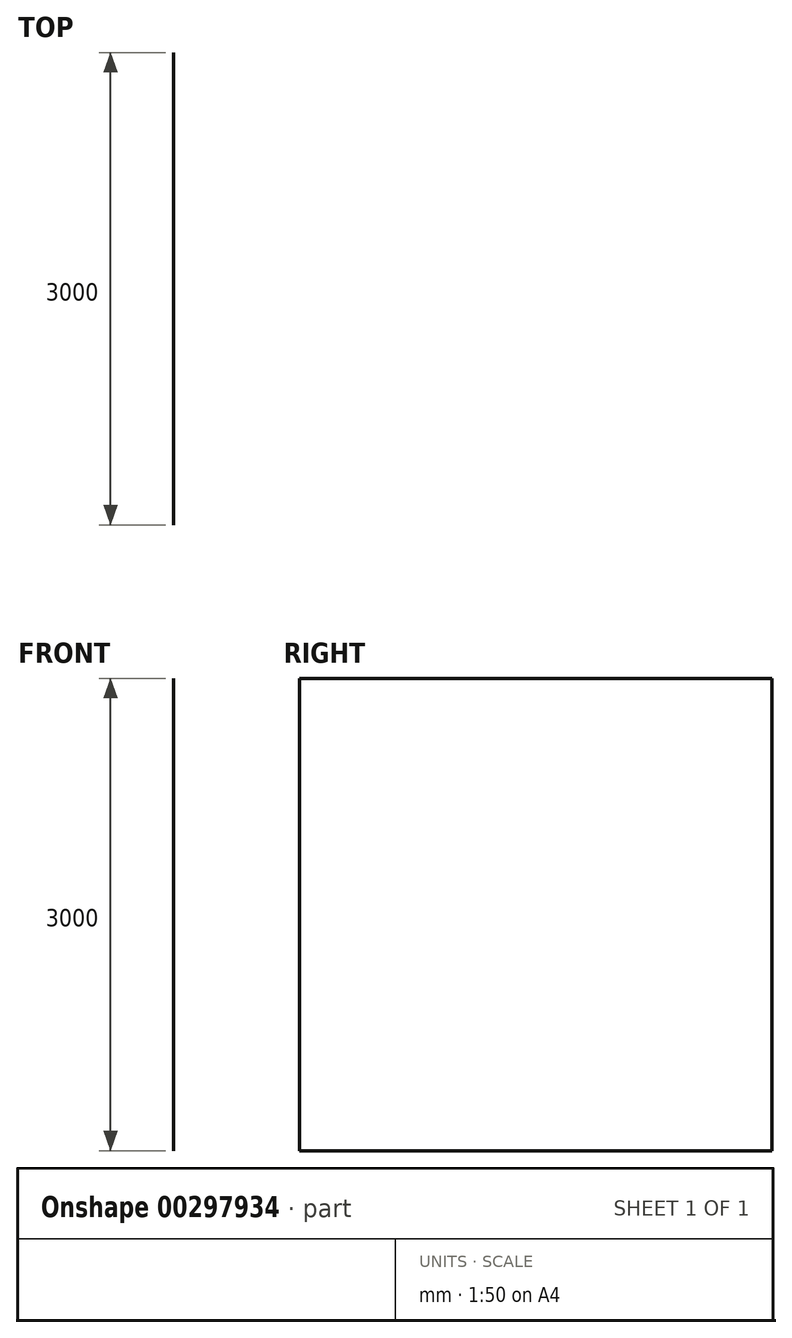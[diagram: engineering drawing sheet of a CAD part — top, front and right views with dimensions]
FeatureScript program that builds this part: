
annotation { "Feature Type Name" : "Feature", "Feature Type Description" : "" }
export const myFeature = defineFeature(function(context is Context, id is Id, definition is map)
    precondition{}
    {
        {
            var Q0;
            Q0=qCreatedBy(makeId("Top.planeOp"),FACE);
            var sketch = newSketch(context, id + "F0", { "sketchPlane" : qUnion([Q0])});
            skPoint(sketch, "E0.middle", {"position": v(0, 0) * mm});
            skLineSegment(sketch, "E1", {"start": v(0, -1500) * mm, "end": v(0, 1500) * mm});
            skSolve(sketch);
        }
        {
            var Q0;
            Q0=sQuery(id+"F0.wireOp",EDGE,"E1");
            extrude(context, id + "F1", {"bodyType" : ToolBodyType.SURFACE, "surfaceEntities" : qUnion([Q0]), "endBound" : BoundingType.SYMMETRIC, "depth" : 3000 * mm});
        }
    });
